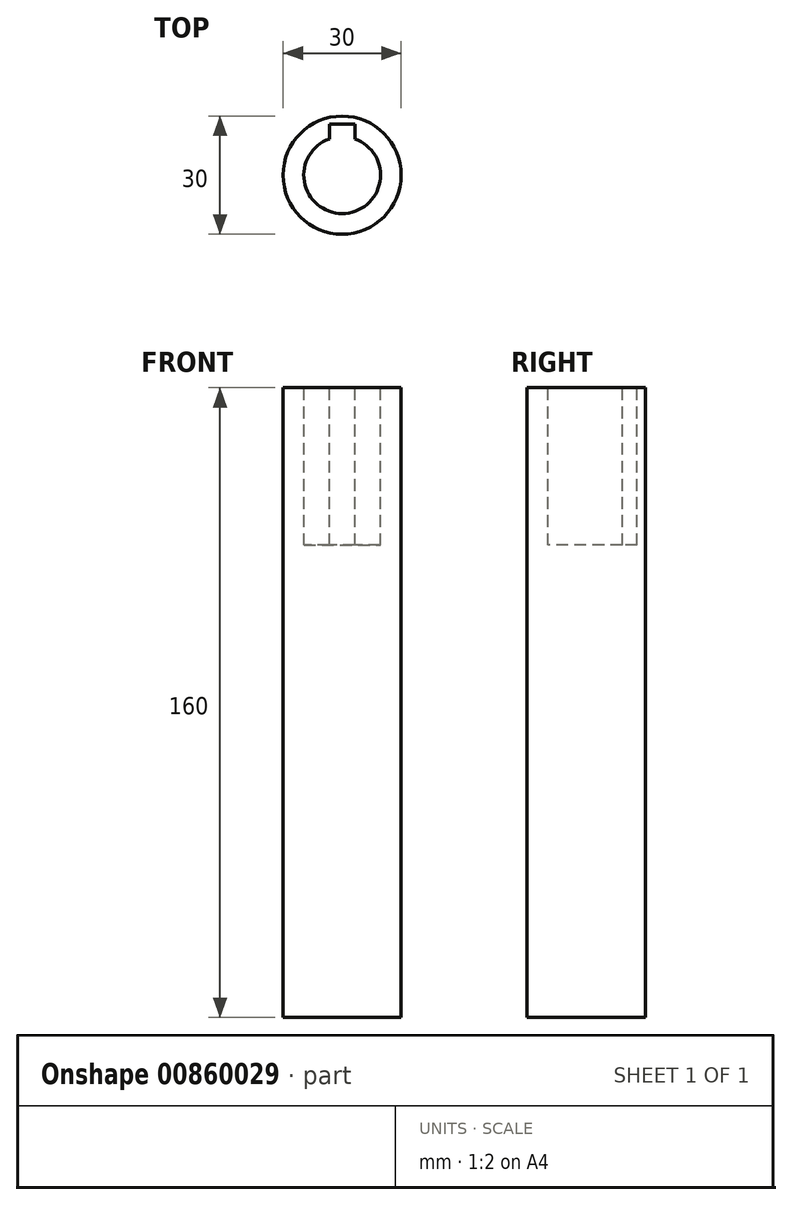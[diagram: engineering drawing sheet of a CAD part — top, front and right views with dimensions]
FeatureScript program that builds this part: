
annotation { "Feature Type Name" : "Feature", "Feature Type Description" : "" }
export const myFeature = defineFeature(function(context is Context, id is Id, definition is map)
    precondition{}
    {
        {
            var Q0;
            Q0=qCreatedBy(makeId("Top.planeOp"),FACE);
            var sketch = newSketch(context, id + "F0", { "sketchPlane" : qUnion([Q0])});
            skCircle(sketch, "E0", {"center": v(0, 0) * mm, "radius": 15 * mm});
            skSolve(sketch);
        }
        {
            var Q0;
            Q0=qSketchRegion(id+"F0",true);
            var Q1;
            Q1 = qSketchRegion(id + "F2", true);
            extrude(context, id + "F1", {"entities" : qUnion([Q0, Q1]), "depth" : 160 * mm, "offsetDistance" : 25 * mm});
        }
        {
            var Q0;
            Q0=makeQuery(id+"F1.opExtrude","CAP_FACE",FACE,{"disambiguationData":[OSD([sQuery(id+"F0.wireOp",EDGE,"E0")])],"isStart":false});
            var sketch = newSketch(context, id + "F2", { "sketchPlane" : qUnion([Q0])});
            skCircle(sketch, "E1", {"center": v(0, 0) * mm, "radius": 9.75 * mm});
            skLineSegment(sketch, "E2.bottom", {"start": v(3.25, 12.95) * mm, "end": v(-3.25, 12.95) * mm});
            skLineSegment(sketch, "E2.top", {"start": v(3.25, 6.55) * mm, "end": v(-3.25, 6.55) * mm});
            skLineSegment(sketch, "E2.left", {"start": v(3.25, 12.95) * mm, "end": v(3.25, 6.55) * mm});
            skLineSegment(sketch, "E2.right", {"start": v(-3.25, 12.95) * mm, "end": v(-3.25, 6.55) * mm});
            skPoint(sketch, "E2.middle", {"position": v(0, 9.75) * mm});
            skSolve(sketch);
        }
        {
            var Q0;
            Q0=qSketchRegion(id+"F2",true);
            extrude(context, id + "F3", {"entities" : qUnion([Q0]), "operationType" : NewBodyOperationType.REMOVE, "oppositeDirection" : true, "depth" : 40 * mm, "offsetDistance" : 25 * mm});
        }
    });
